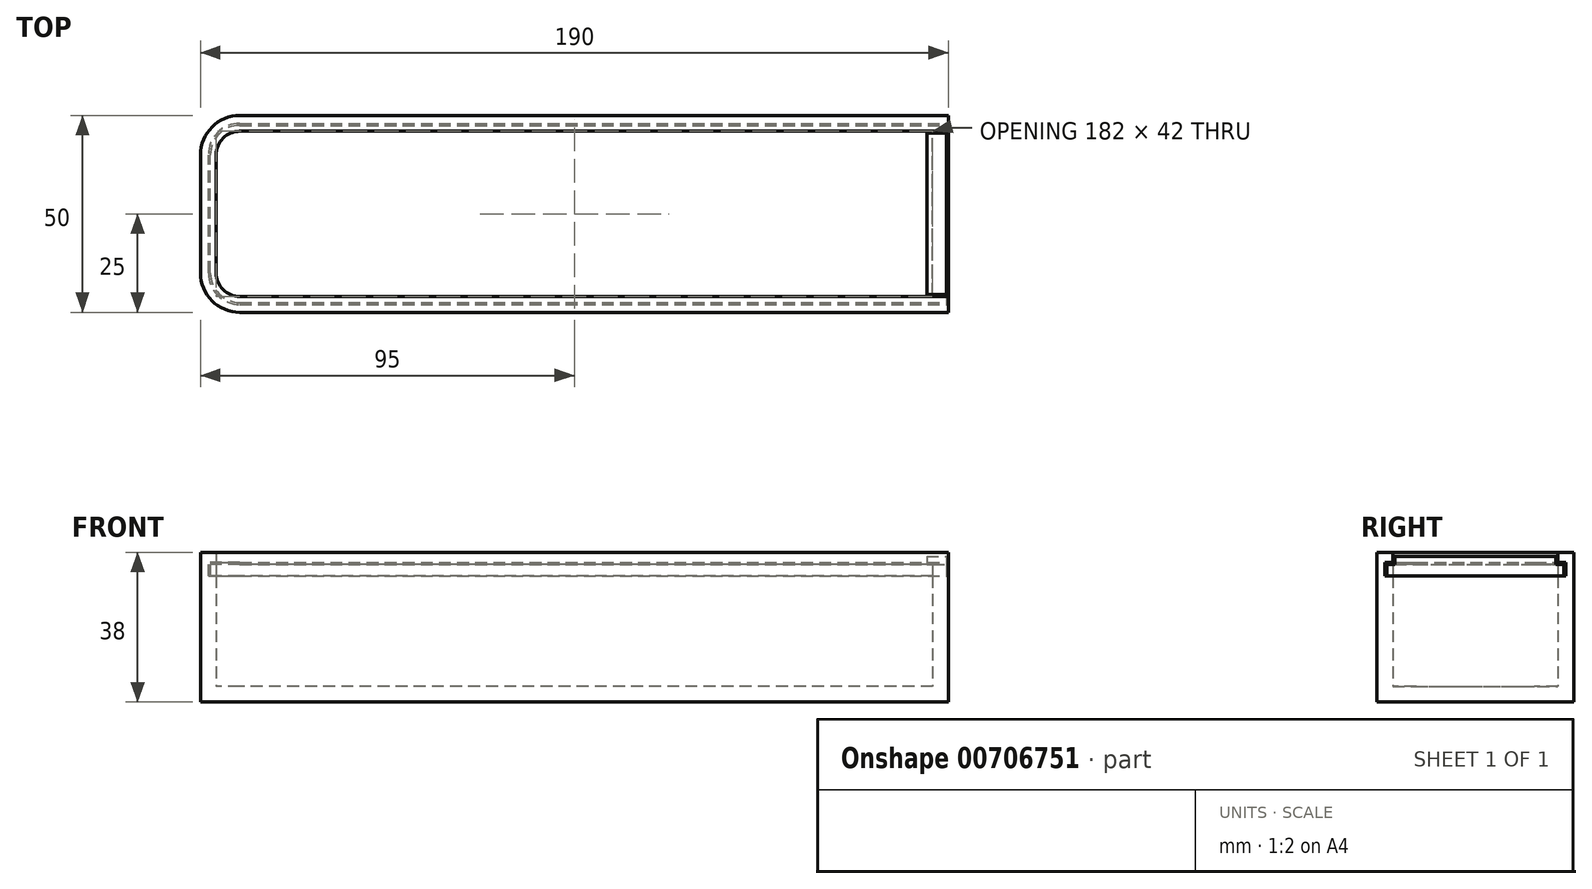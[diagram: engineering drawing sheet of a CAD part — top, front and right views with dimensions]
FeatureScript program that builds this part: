
annotation { "Feature Type Name" : "Feature", "Feature Type Description" : "" }
export const myFeature = defineFeature(function(context is Context, id is Id, definition is map)
    precondition{}
    {
        {
            var Q0;
            Q0=qCreatedBy(makeId("Top.planeOp"),FACE);
            var sketch = newSketch(context, id + "F0", { "sketchPlane" : qUnion([Q0])});
            skLineSegment(sketch, "E0.bottom", {"start": v(91, -21) * mm, "end": v(-85, -21) * mm});
            skLineSegment(sketch, "E0.top", {"start": v(91, 21) * mm, "end": v(-85, 21) * mm});
            skLineSegment(sketch, "E0.left", {"start": v(91, -21) * mm, "end": v(91, 21) * mm});
            skLineSegment(sketch, "E0.right", {"start": v(-91, -15) * mm, "end": v(-91, 15) * mm});
            skPoint(sketch, "E0.middle", {"position": v(0, 0) * mm});
            skPoint(sketch, "E1.visualSharp", {"position": v(91, -21) * mm});
            skPoint(sketch, "E2.visualSharp", {"position": v(91, 21) * mm});
            skPoint(sketch, "E3.visualSharp", {"position": v(-91, 21) * mm});
            skArc(sketch, "E3.filletArc", {"start": v(-85, 21) * mm, "mid": v(-89.24, 19.24) * mm, "end": v(-91, 15) * mm});
            skPoint(sketch, "E4.visualSharp", {"position": v(-91, -21) * mm});
            skArc(sketch, "E4.filletArc", {"start": v(-91, -15) * mm, "mid": v(-89.24, -19.24) * mm, "end": v(-85, -21) * mm});
            skLineSegment(sketch, "E5.bottom", {"start": v(95, -25) * mm, "end": v(-85, -25) * mm});
            skLineSegment(sketch, "E5.top", {"start": v(95, 25) * mm, "end": v(-85, 25) * mm});
            skLineSegment(sketch, "E5.left", {"start": v(95, -25) * mm, "end": v(95, 25) * mm});
            skLineSegment(sketch, "E5.right", {"start": v(-95, -15) * mm, "end": v(-95, 15) * mm});
            skPoint(sketch, "E6.visualSharp", {"position": v(95, -25) * mm});
            skPoint(sketch, "E7.visualSharp", {"position": v(-95, -25) * mm});
            skArc(sketch, "E7.filletArc", {"start": v(-95, -15) * mm, "mid": v(-92.07, -22.07) * mm, "end": v(-85, -25) * mm});
            skPoint(sketch, "E8.visualSharp", {"position": v(-95, 25) * mm});
            skArc(sketch, "E8.filletArc", {"start": v(-85, 25) * mm, "mid": v(-92.07, 22.07) * mm, "end": v(-95, 15) * mm});
            skPoint(sketch, "E9.visualSharp", {"position": v(95, 25) * mm});
            skLineSegment(sketch, "E10", {"start": v(-91, 15) * mm, "end": v(-95, 15) * mm});
            skLineSegment(sketch, "E11", {"start": v(-85, 21) * mm, "end": v(-85, 25) * mm});
            skSolve(sketch);
        }
        {
            var Q0;
            Q0=makeQuery(id+"F0.imprint","IMPRINT",FACE,{"disambiguationData":[TD([[makeQuery(id+"F0.imprint","IMPRINT",EDGE,{"derivedFrom":sQuery(id+"F0.wireOp",EDGE,"E3.filletArc")}),-1.0]])]});
            var Q1;
            Q1=makeQuery(id+"F0.imprint","IMPRINT",FACE,{"disambiguationData":[TD([[makeQuery(id+"F0.imprint","IMPRINT",EDGE,{"derivedFrom":sQuery(id+"F0.wireOp",EDGE,"E0.bottom")}),1.0]])]});
            var Q2;
            Q2=makeQuery(id+"F0.imprint","IMPRINT",FACE,{"disambiguationData":[TD([[makeQuery(id+"F0.imprint","IMPRINT",EDGE,{"derivedFrom":sQuery(id+"F0.wireOp",EDGE,"JrD6cjlr-IqBT-4h7f-Q6kM-MQEMmFK3sbHS")}),1.0]])]});
            extrude(context, id + "F1", {"entities" : qUnion([Q0, Q1, Q2]), "depth" : 38 * mm, "offsetDistance" : 25 * mm});
        }
        {
            var Q0;
            Q0=makeQuery(id+"F0.imprint","IMPRINT",FACE,{"disambiguationData":[TD([[makeQuery(id+"F0.imprint","IMPRINT",EDGE,{"derivedFrom":sQuery(id+"F0.wireOp",EDGE,"E0.bottom")}),-1.0]])]});
            extrude(context, id + "F2", {"entities" : qUnion([Q0]), "operationType" : NewBodyOperationType.ADD, "depth" : 4 * mm, "offsetDistance" : 25 * mm});
        }
        {
            var Q0;
            Q0=makeQuery(id+"F1.opExtrude","SWEPT_FACE",FACE,{"disambiguationData":[OSD([sQuery(id+"F0.wireOp",EDGE,"E5.left")])]});
            var sketch = newSketch(context, id + "F3", { "sketchPlane" : qUnion([Q0])});
            skLineSegment(sketch, "E12.bottom", {"start": v(-21, 38) * mm, "end": v(21, 38) * mm});
            skLineSegment(sketch, "E12.top", {"start": v(-21, 32) * mm, "end": v(21, 32) * mm});
            skLineSegment(sketch, "E12.left", {"start": v(-21, 38) * mm, "end": v(-21, 35.5) * mm});
            skLineSegment(sketch, "E12.right", {"start": v(21, 38) * mm, "end": v(21, 35.5) * mm});
            skLineSegment(sketch, "E13.bottom", {"start": v(-21, 32) * mm, "end": v(-23, 32) * mm});
            skLineSegment(sketch, "E13.top", {"start": v(-21, 35.5) * mm, "end": v(-23, 35.5) * mm});
            skLineSegment(sketch, "E13.right", {"start": v(-23, 32) * mm, "end": v(-23, 35.5) * mm});
            skLineSegment(sketch, "E14", {"start": v(0, 38) * mm, "end": v(0, 32) * mm, "construction": true});
            skLineSegment(sketch, "E15.MirrorCS", {"start": v(21, 32) * mm, "end": v(23, 32) * mm});
            skLineSegment(sketch, "E16.MirrorCS", {"start": v(21, 35.5) * mm, "end": v(23, 35.5) * mm});
            skLineSegment(sketch, "E17.MirrorCS", {"start": v(23, 32) * mm, "end": v(23, 35.5) * mm});
            skLineSegment(sketch, "E18", {"start": v(-21, 35.5) * mm, "end": v(21, 35.5) * mm});
            skSolve(sketch);
        }
        {
            var Q0;
            Q0=makeQuery(id+"F3.imprint","IMPRINT",FACE,{"disambiguationData":[TD([[makeQuery(id+"F3.imprint","IMPRINT",EDGE,{"derivedFrom":sQuery(id+"F3.wireOp",EDGE,"E12.bottom")}),-1.0]])]});
            var Q1;
            Q1=makeQuery(id+"F3.imprint","IMPRINT",FACE,{"disambiguationData":[TD([[makeQuery(id+"F3.imprint","IMPRINT",EDGE,{"derivedFrom":sQuery(id+"F3.wireOp",EDGE,"E12.top")}),1.0]])]});
            var Q2;
            Q2=makeQuery(id+"F1.opExtrude","CAP_VERTEX",VERTEX,{"disambiguationData":[OSD([sQuery(id+"F0.wireOp",EDGE,"E5.top"),sQuery(id+"F0.wireOp",EDGE,"E8.filletArc"),sQuery(id+"F0.wireOp",EDGE,"E11")])],"isStart":false});
            extrude(context, id + "F4", {"entities" : qUnion([Q0, Q1]), "operationType" : NewBodyOperationType.REMOVE, "endBound" : BoundingType.UP_TO_VERTEX, "oppositeDirection" : true, "depth" : 25 * mm, "endBoundEntityVertex" : qUnion([Q2]), "offsetDistance" : 25 * mm});
        }
        {
            var Q0;
            {var subQ0=sQuery(id+"F3.wireOp",EDGE,"E15.MirrorCS");var subQ1=sQuery(id+"F3.wireOp",EDGE,"E13.bottom");var subQ2=sQuery(id+"F3.wireOp",EDGE,"E12.top");var subQ3=sQuery(id+"F3.wireOp",EDGE,"E12.left");var subQ4=sQuery(id+"F3.wireOp",EDGE,"E13.top");var subQ5=sQuery(id+"F3.wireOp",EDGE,"E13.right");Q0=makeQuery(id+"F4.boolean.opBoolean","COPY",FACE,{"disambiguationData":[TD([makeQuery(id+"F1.opExtrude","SWEPT_FACE",FACE,{"disambiguationData":[OSD([sQuery(id+"F0.wireOp",EDGE,"E0.bottom")])]})])],"derivedFrom":makeQuery(id+"F4.opExtrude","CAP_FACE",FACE,{"disambiguationData":[OSD([sQuery(id+"F3.wireOp",EDGE,"E12.bottom"),subQ2,subQ3,sQuery(id+"F3.wireOp",EDGE,"E12.right"),subQ1,subQ4,subQ5,subQ0,sQuery(id+"F3.wireOp",EDGE,"E16.MirrorCS"),sQuery(id+"F3.wireOp",EDGE,"E17.MirrorCS")])],"isStart":false})});}
            var sketch = newSketch(context, id + "F5", { "sketchPlane" : qUnion([Q0])});
            skLineSegment(sketch, "E19.bottom", {"start": v(-21, 32) * mm, "end": v(-23, 32) * mm});
            skLineSegment(sketch, "E19.top", {"start": v(-21, 35.5) * mm, "end": v(-23, 35.5) * mm});
            skLineSegment(sketch, "E19.left", {"start": v(-21, 32) * mm, "end": v(-21, 35.5) * mm});
            skLineSegment(sketch, "E19.right", {"start": v(-23, 32) * mm, "end": v(-23, 35.5) * mm});
            skSolve(sketch);
        }
        {
            var Q0;
            Q0=makeQuery(id+"F5.imprint","IMPRINT",FACE,{"disambiguationData":[TD([[makeQuery(id+"F5.imprint","IMPRINT",EDGE,{"derivedFrom":sQuery(id+"F5.wireOp",EDGE,"E19.bottom")}),-1.0]])]});
            var Q1;
            Q1=makeQuery(id+"F1.opExtrude","CAP_EDGE",EDGE,{"disambiguationData":[OSD([sQuery(id+"F0.wireOp",EDGE,"E4.filletArc")])],"isStart":false});
            var Q2;
            Q2=makeQuery(id+"F1.opExtrude","CAP_EDGE",EDGE,{"disambiguationData":[OSD([sQuery(id+"F0.wireOp",EDGE,"E0.right")])],"isStart":false});
            var Q3;
            Q3=makeQuery(id+"F1.opExtrude","CAP_EDGE",EDGE,{"disambiguationData":[OSD([sQuery(id+"F0.wireOp",EDGE,"E3.filletArc")])],"isStart":false});
            sweep(context, id + "F6", {"operationType" : NewBodyOperationType.REMOVE, "profiles" : qUnion([Q0]), "path" : qUnion([Q1, Q2, Q3])});
        }
        {
            var Q0;
            Q0=makeQuery(id+"F6.boolean.opBoolean","MERGE",FACE,{"derivedFrom":[makeQuery(id+"F4.boolean.opBoolean","COPY",FACE,{"derivedFrom":makeQuery(id+"F4.opExtrude","SWEPT_FACE",FACE,{"disambiguationData":[OSD([sQuery(id+"F3.wireOp",EDGE,"E12.top"),sQuery(id+"F3.wireOp",EDGE,"E13.bottom"),sQuery(id+"F3.wireOp",EDGE,"E15.MirrorCS")])]})})],"fromTools":[makeQuery(id+"F6.opSweep","SWEPT_FACE",FACE,{"disambiguationData":[OSD([sQuery(id+"F0.wireOp",EDGE,"E4.filletArc"),sQuery(id+"F5.wireOp",EDGE,"E19.bottom")])]})]});
            var sketch = newSketch(context, id + "F7", { "sketchPlane" : qUnion([Q0])});
            skLineSegment(sketch, "E20.0", {"start": v(-85, -23) * mm, "end": v(95, -23) * mm});
            skLineSegment(sketch, "E21.0", {"start": v(95, 23) * mm, "end": v(95, -23) * mm});
            skArc(sketch, "E22.0", {"start": v(-85, -23) * mm, "mid": v(-90.66, -20.66) * mm, "end": v(-93, -15) * mm});
            skLineSegment(sketch, "E23.0", {"start": v(-93, -15) * mm, "end": v(-93, 15) * mm});
            skArc(sketch, "E24.0", {"start": v(-93, 15) * mm, "mid": v(-90.66, 20.66) * mm, "end": v(-85, 23) * mm});
            skLineSegment(sketch, "E25.0", {"start": v(-85, 23) * mm, "end": v(95, 23) * mm});
            skLineSegment(sketch, "E26.0", {"start": v(-85, 22.5) * mm, "end": v(94.5, 22.5) * mm});
            skLineSegment(sketch, "E26.1", {"start": v(-85, -22.5) * mm, "end": v(94.5, -22.5) * mm});
            skArc(sketch, "E26.2", {"start": v(-85, -22.5) * mm, "mid": v(-90.3, -20.3) * mm, "end": v(-92.5, -15) * mm});
            skLineSegment(sketch, "E26.3", {"start": v(94.5, 22.5) * mm, "end": v(94.5, -22.5) * mm});
            skLineSegment(sketch, "E26.4", {"start": v(-92.5, -15) * mm, "end": v(-92.5, 15) * mm});
            skArc(sketch, "E26.5", {"start": v(-92.5, 15) * mm, "mid": v(-90.3, 20.3) * mm, "end": v(-85, 22.5) * mm});
            skSolve(sketch);
        }
        {
            var Q0;
            Q0=makeQuery(id+"F7.imprint","IMPRINT",FACE,{"disambiguationData":[TD([[makeQuery(id+"F7.imprint","IMPRINT",EDGE,{"derivedFrom":sQuery(id+"F7.wireOp",EDGE,"E26.0")}),-1.0]])]});
            var Q1;
            {var subQ0=sQuery(id+"F5.wireOp",EDGE,"E19.left");var subQ1=sQuery(id+"F5.wireOp",EDGE,"E19.bottom");Q1=makeQuery(id+"F7.imprint","IMPRINT",FACE,{"disambiguationData":[TD([[makeQuery(id+"F7.imprint","IMPRINT",EDGE,{"derivedFrom":makeQuery(id+"F6.boolean.opBoolean","COPY",EDGE,{"derivedFrom":makeQuery(id+"F6.opSweep","SWEPT_EDGE",EDGE,{"disambiguationData":[OSD([sQuery(id+"F0.wireOp",EDGE,"E0.right"),subQ1,subQ0])]})})}),-1.0]])]});}
            extrude(context, id + "F8", {"entities" : qUnion([Q0, Q1]), "depth" : 3 * mm, "offsetDistance" : 25 * mm});
        }
        {
            var Q0;
            Q0=makeQuery(id+"F8.opExtrude","CAP_FACE",FACE,{"disambiguationData":[OSD([sQuery(id+"F7.wireOp",EDGE,"E26.0"),sQuery(id+"F7.wireOp",EDGE,"E26.1"),sQuery(id+"F7.wireOp",EDGE,"E26.2"),sQuery(id+"F7.wireOp",EDGE,"E26.3"),sQuery(id+"F7.wireOp",EDGE,"E26.4"),sQuery(id+"F7.wireOp",EDGE,"E26.5")])],"isStart":false});
            var sketch = newSketch(context, id + "F9", { "sketchPlane" : qUnion([Q0])});
            skLineSegment(sketch, "E27.bottom", {"start": v(89.5, -20.5) * mm, "end": v(94.5, -20.5) * mm});
            skLineSegment(sketch, "E27.top", {"start": v(89.5, 20.5) * mm, "end": v(94.5, 20.5) * mm});
            skLineSegment(sketch, "E27.left", {"start": v(89.5, -20.5) * mm, "end": v(89.5, 20.5) * mm});
            skLineSegment(sketch, "E27.right", {"start": v(94.5, -20.5) * mm, "end": v(94.5, 20.5) * mm});
            skSolve(sketch);
        }
        {
            var Q0;
            Q0 = qSketchRegion(id + "F9", true);
            var Q1;
            Q1=makeQuery(id+"F1.opExtrude","CAP_FACE",FACE,{"disambiguationData":[OSD([sQuery(id+"F0.wireOp",EDGE,"E0.bottom"),sQuery(id+"F0.wireOp",EDGE,"E0.top"),sQuery(id+"F0.wireOp",EDGE,"E0.left"),sQuery(id+"F0.wireOp",EDGE,"E0.right"),sQuery(id+"F0.wireOp",EDGE,"E3.filletArc"),sQuery(id+"F0.wireOp",EDGE,"E4.filletArc"),sQuery(id+"F0.wireOp",EDGE,"E5.bottom"),sQuery(id+"F0.wireOp",EDGE,"E5.top"),sQuery(id+"F0.wireOp",EDGE,"E5.left"),sQuery(id+"F0.wireOp",EDGE,"E5.right"),sQuery(id+"F0.wireOp",EDGE,"E7.filletArc"),sQuery(id+"F0.wireOp",EDGE,"E8.filletArc")])],"isStart":false});
            extrude(context, id + "F10", {"entities" : qUnion([Q0]), "operationType" : NewBodyOperationType.ADD, "endBound" : BoundingType.UP_TO_SURFACE, "depth" : 25 * mm, "endBoundEntityFace" : qUnion([Q1]), "hasOffset" : true, "offsetDistance" : 1 * mm});
        }
    });
